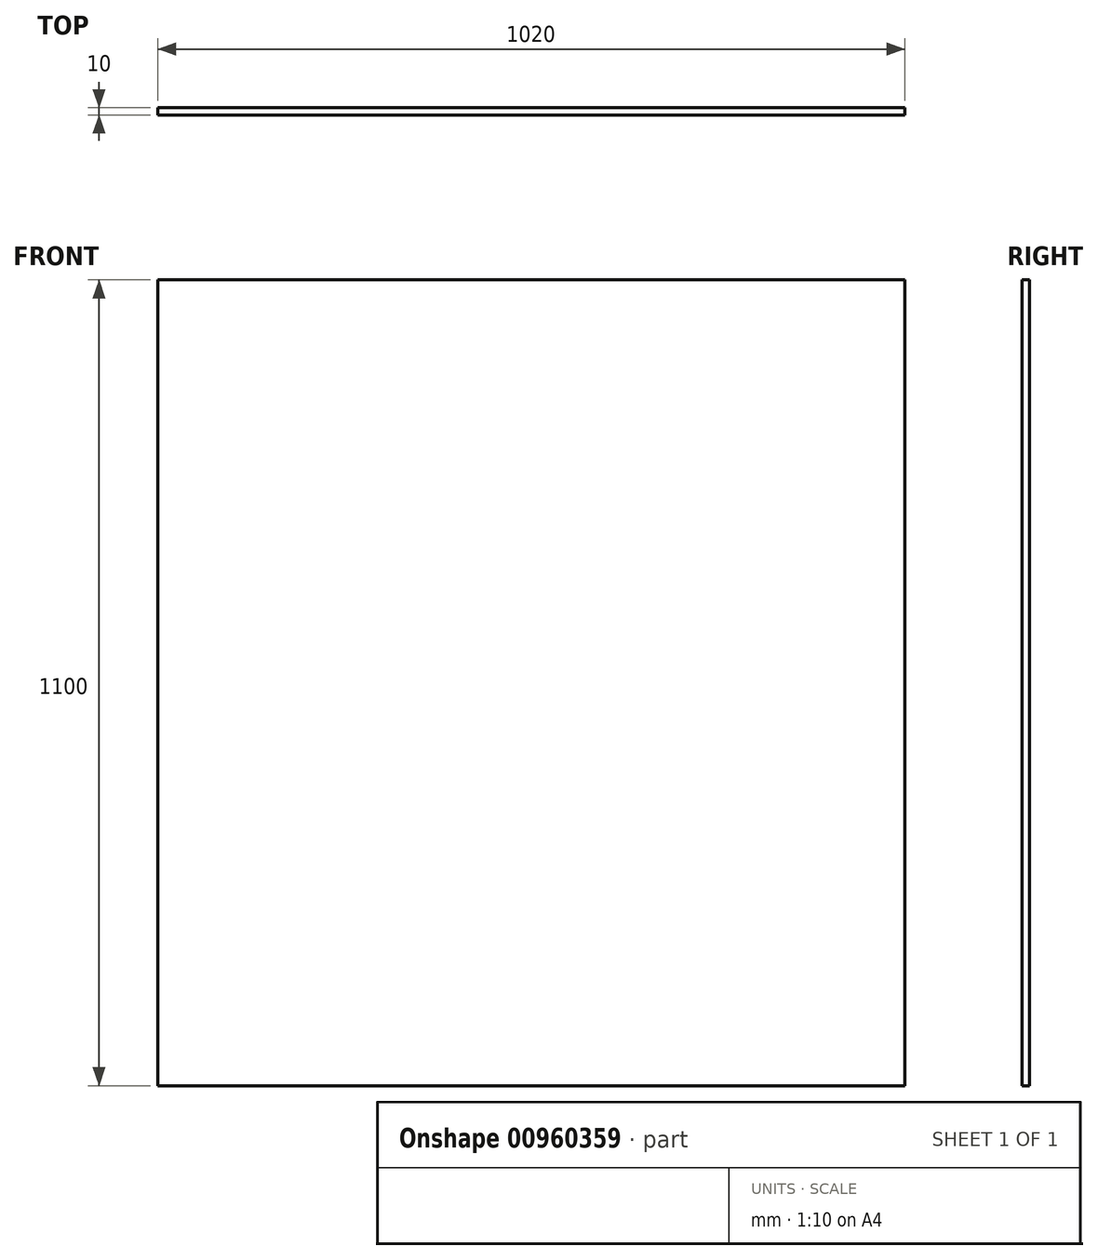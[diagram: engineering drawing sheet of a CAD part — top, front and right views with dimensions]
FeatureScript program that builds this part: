
annotation { "Feature Type Name" : "Feature", "Feature Type Description" : "" }
export const myFeature = defineFeature(function(context is Context, id is Id, definition is map)
    precondition{}
    {
        {
            var Q0;
            Q0=qCreatedBy(makeId("Front.planeOp"),FACE);
            var sketch = newSketch(context, id + "F0", { "sketchPlane" : qUnion([Q0])});
            skLineSegment(sketch, "E0.bottom", {"start": v(-510, 550) * mm, "end": v(510, 550) * mm});
            skLineSegment(sketch, "E0.top", {"start": v(-510, -550) * mm, "end": v(510, -550) * mm});
            skLineSegment(sketch, "E0.left", {"start": v(-510, 550) * mm, "end": v(-510, -550) * mm});
            skLineSegment(sketch, "E0.right", {"start": v(510, 550) * mm, "end": v(510, -550) * mm});
            skPoint(sketch, "E0.middle", {"position": v(0, 0) * mm});
            skSolve(sketch);
        }
        {
            var Q0;
            Q0 = qSketchRegion(id + "F0", true);
            extrude(context, id + "F1", {"entities" : qUnion([Q0]), "depth" : 10 * mm, "offsetDistance" : 25 * mm});
        }
    });
